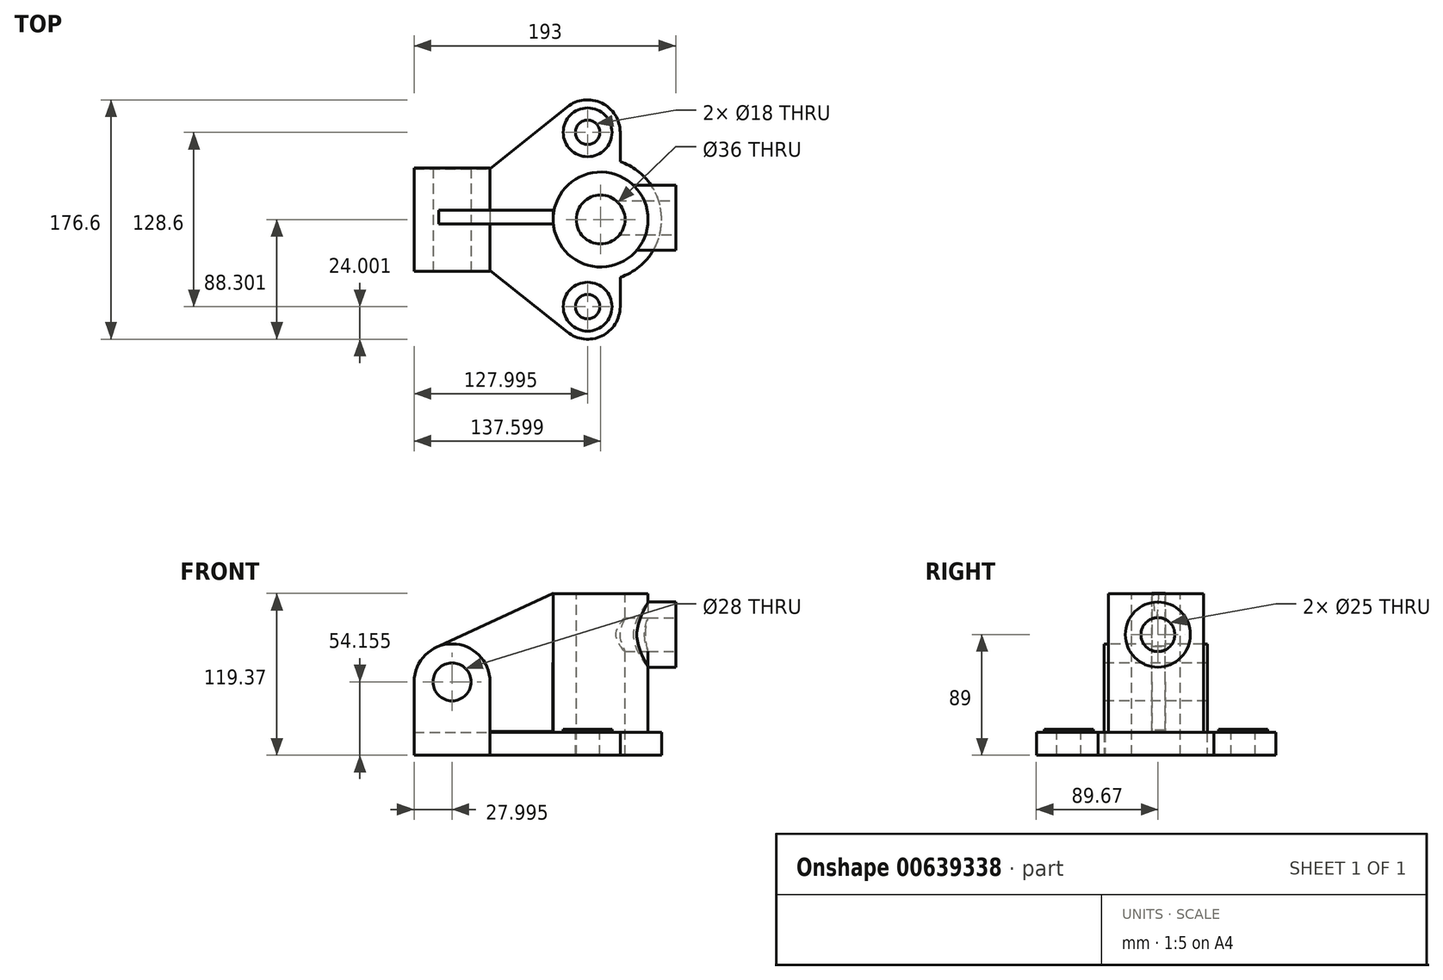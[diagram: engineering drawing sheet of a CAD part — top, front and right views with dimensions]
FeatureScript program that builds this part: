
annotation { "Feature Type Name" : "Feature", "Feature Type Description" : "" }
export const myFeature = defineFeature(function(context is Context, id is Id, definition is map)
    precondition{}
    {
        {
            var Q0;
            Q0=qCreatedBy(makeId("Top.planeOp"),FACE);
            var sketch = newSketch(context, id + "F0", { "sketchPlane" : qUnion([Q0])});
            skLineSegment(sketch, "E0.bottom", {"start": v(-54.34, 30.78) * mm, "end": v(1.66, 30.78) * mm});
            skLineSegment(sketch, "E0.top", {"start": v(-54.34, -44.22) * mm, "end": v(1.66, -44.22) * mm});
            skLineSegment(sketch, "E0.left", {"start": v(-54.34, 30.78) * mm, "end": v(-54.34, -44.22) * mm});
            skLineSegment(sketch, "E0.right", {"start": v(1.66, 30.78) * mm, "end": v(1.66, -44.22) * mm});
            skLineSegment(sketch, "E1", {"start": v(1.66, -44.22) * mm, "end": v(58.68, -89.77) * mm});
            skLineSegment(sketch, "E2", {"start": v(1.66, 30.78) * mm, "end": v(58.68, 76.33) * mm});
            skArc(sketch, "E3", {"start": v(58.68, 76.33) * mm, "mid": v(84.06, 79.2) * mm, "end": v(97.66, 57.58) * mm});
            skArc(sketch, "E4", {"start": v(58.68, -89.77) * mm, "mid": v(84.06, -92.65) * mm, "end": v(97.66, -71.02) * mm});
            skLineSegment(sketch, "E5", {"start": v(97.66, -71.02) * mm, "end": v(97.66, -49.35) * mm});
            skLineSegment(sketch, "E6", {"start": v(97.66, 57.58) * mm, "end": v(97.66, 35.92) * mm});
            skArc(sketch, "E7", {"start": v(97.66, -49.35) * mm, "mid": v(128.26, -6.72) * mm, "end": v(97.66, 35.92) * mm});
            skSolve(sketch);
        }
        {
            var Q0;
            Q0 = qSketchRegion(id + "F0", true);
            extrude(context, id + "F1", {"entities" : qUnion([Q0]), "depth" : 17 * mm, "offsetDistance" : 25.4 * mm});
        }
        {
            var Q0;
            Q0=makeQuery(id+"F1.opExtrude","CAP_FACE",FACE,{"disambiguationData":[OSD([sQuery(id+"F0.wireOp",EDGE,"E0.bottom"),sQuery(id+"F0.wireOp",EDGE,"E0.top"),sQuery(id+"F0.wireOp",EDGE,"E0.left"),sQuery(id+"F0.wireOp",EDGE,"E1"),sQuery(id+"F0.wireOp",EDGE,"E2"),sQuery(id+"F0.wireOp",EDGE,"E3"),sQuery(id+"F0.wireOp",EDGE,"E4"),sQuery(id+"F0.wireOp",EDGE,"E5"),sQuery(id+"F0.wireOp",EDGE,"E6"),sQuery(id+"F0.wireOp",EDGE,"E7")])],"isStart":false});
            var sketch = newSketch(context, id + "F2", { "sketchPlane" : qUnion([Q0])});
            skCircle(sketch, "E8", {"center": v(73.66, 57.58) * mm, "radius": 18 * mm});
            skCircle(sketch, "E9", {"center": v(73.66, -71.02) * mm, "radius": 18 * mm});
            skSolve(sketch);
        }
        {
            var Q0;
            Q0 = qSketchRegion(id + "F2", true);
            extrude(context, id + "F3", {"entities" : qUnion([Q0]), "operationType" : NewBodyOperationType.ADD, "depth" : 2 * mm, "offsetDistance" : 25.4 * mm});
        }
        {
            var Q0;
            Q0=makeQuery(id+"F3.opExtrude","CAP_FACE",FACE,{"disambiguationData":[OSD([sQuery(id+"F2.wireOp",EDGE,"E9")])],"isStart":false});
            var sketch = newSketch(context, id + "F4", { "sketchPlane" : qUnion([Q0])});
            skCircle(sketch, "E10", {"center": v(73.66, -71.02) * mm, "radius": 9 * mm});
            skCircle(sketch, "E11", {"center": v(73.66, 57.58) * mm, "radius": 9 * mm});
            skSolve(sketch);
        }
        {
            var Q0;
            Q0 = qSketchRegion(id + "F4", true);
            extrude(context, id + "F5", {"entities" : qUnion([Q0]), "operationType" : NewBodyOperationType.REMOVE, "oppositeDirection" : true, "depth" : 25.4 * mm, "offsetDistance" : 25.4 * mm});
        }
        {
            var Q0;
            Q0=makeQuery(id+"F1.opExtrude","CAP_FACE",FACE,{"disambiguationData":[OSD([sQuery(id+"F0.wireOp",EDGE,"E0.bottom"),sQuery(id+"F0.wireOp",EDGE,"E0.top"),sQuery(id+"F0.wireOp",EDGE,"E0.left"),sQuery(id+"F0.wireOp",EDGE,"E1"),sQuery(id+"F0.wireOp",EDGE,"E2"),sQuery(id+"F0.wireOp",EDGE,"E3"),sQuery(id+"F0.wireOp",EDGE,"E4"),sQuery(id+"F0.wireOp",EDGE,"E5"),sQuery(id+"F0.wireOp",EDGE,"E6"),sQuery(id+"F0.wireOp",EDGE,"E7")])],"isStart":false});
            var sketch = newSketch(context, id + "F6", { "sketchPlane" : qUnion([Q0])});
            skCircle(sketch, "E12", {"center": v(83.26, -6.72) * mm, "radius": 35 * mm});
            skSolve(sketch);
        }
        {
            var Q0;
            Q0 = qSketchRegion(id + "F6", true);
            extrude(context, id + "F7", {"entities" : qUnion([Q0]), "operationType" : NewBodyOperationType.ADD, "depth" : 102 * mm, "offsetDistance" : 25.4 * mm});
        }
        {
            var Q0;
            Q0=makeQuery(id+"F7.opExtrude","CAP_FACE",FACE,{"disambiguationData":[OSD([sQuery(id+"F6.wireOp",EDGE,"E12")])],"isStart":false});
            var sketch = newSketch(context, id + "F8", { "sketchPlane" : qUnion([Q0])});
            skCircle(sketch, "E13", {"center": v(83.26, -6.72) * mm, "radius": 18 * mm});
            skSolve(sketch);
        }
        {
            var Q0;
            Q0 = qSketchRegion(id + "F8", true);
            extrude(context, id + "F9", {"entities" : qUnion([Q0]), "operationType" : NewBodyOperationType.REMOVE, "oppositeDirection" : true, "depth" : 128.52 * mm, "offsetDistance" : 25.4 * mm});
        }
        {
            var Q0;
            Q0=makeQuery(id+"F1.opExtrude","SWEPT_FACE",FACE,{"disambiguationData":[OSD([sQuery(id+"F0.wireOp",EDGE,"E0.top")])]});
            extrude(context, id + "F10", {"entities" : qUnion([Q0]), "operationType" : NewBodyOperationType.ADD, "depth" : 0.76 * mm, "offsetDistance" : 25.4 * mm});
        }
        {
            var Q0;
            Q0=makeQuery(id+"F10.opExtrude","CAP_FACE",FACE,{"disambiguationData":[OSD([sQuery(id+"F0.wireOp",EDGE,"E0.top")])],"isStart":false});
            var sketch = newSketch(context, id + "F11", { "sketchPlane" : qUnion([Q0])});
            skLineSegment(sketch, "E14", {"start": v(-54.34, 8.5) * mm, "end": v(-54.34, 54.16) * mm});
            skPoint(sketch, "E14.startSnap0", {"position": v(-54.34, 8.5) * mm});
            skArc(sketch, "E15", {"start": v(-54.34, 54.16) * mm, "mid": v(-26.34, 82.16) * mm, "end": v(1.66, 54.16) * mm});
            skLineSegment(sketch, "E16", {"start": v(1.66, 54.16) * mm, "end": v(1.66, 17) * mm});
            skLineSegment(sketch, "E17", {"start": v(1.66, 17) * mm, "end": v(-54.34, 17) * mm});
            skSolve(sketch);
        }
        {
            var Q0;
            Q0 = qSketchRegion(id + "F11", true);
            extrude(context, id + "F12", {"entities" : qUnion([Q0]), "operationType" : NewBodyOperationType.ADD, "oppositeDirection" : true, "depth" : 76.2 * mm, "offsetDistance" : 25.4 * mm});
        }
        {
            var Q0;
            Q0=makeQuery(id+"F12.boolean.opBoolean","MERGE",FACE,{"derivedFrom":[makeQuery(id+"F10.opExtrude","CAP_FACE",FACE,{"disambiguationData":[OSD([sQuery(id+"F0.wireOp",EDGE,"E0.top")])],"isStart":false}),makeQuery(id+"F12.opExtrude","CAP_FACE",FACE,{"disambiguationData":[OSD([sQuery(id+"F11.wireOp",EDGE,"E14"),sQuery(id+"F11.wireOp",EDGE,"E15"),sQuery(id+"F11.wireOp",EDGE,"E16"),sQuery(id+"F11.wireOp",EDGE,"E17")])],"isStart":true})]});
            var sketch = newSketch(context, id + "F13", { "sketchPlane" : qUnion([Q0])});
            skCircle(sketch, "E18", {"center": v(-26.34, 54.16) * mm, "radius": 14 * mm});
            skSolve(sketch);
        }
        {
            var Q0;
            Q0 = qSketchRegion(id + "F13", true);
            extrude(context, id + "F14", {"entities" : qUnion([Q0]), "operationType" : NewBodyOperationType.REMOVE, "oppositeDirection" : true, "depth" : 167.39 * mm, "offsetDistance" : 25.4 * mm});
        }
        {
            var Q0;
            Q0=qCreatedBy(makeId("Front.planeOp"),FACE);
            var sketch = newSketch(context, id + "F15", { "sketchPlane" : qUnion([Q0])});
            skLineSegment(sketch, "E19", {"start": v(48.3, 119.37) * mm, "end": v(-36.3, 80.4) * mm});
            skLineSegment(sketch, "E20", {"start": v(-36.3, 80.4) * mm, "end": v(-5.27, 60.76) * mm});
            skLineSegment(sketch, "E21", {"start": v(-5.27, 60.76) * mm, "end": v(1.8, 17.55) * mm});
            skLineSegment(sketch, "E22", {"start": v(1.8, 17.55) * mm, "end": v(48.04, 17.55) * mm});
            skLineSegment(sketch, "E23", {"start": v(48.04, 17.55) * mm, "end": v(48.3, 119.37) * mm});
            skSolve(sketch);
        }
        {
            var Q0;
            Q0 = qSketchRegion(id + "F15", true);
            extrude(context, id + "F16", {"entities" : qUnion([Q0]), "operationType" : NewBodyOperationType.ADD, "depth" : 9.9 * mm, "offsetDistance" : 25.4 * mm});
        }
        {
            var Q0;
            {var subQ0=sQuery(id+"F0.wireOp",EDGE,"E0.left");Q0=makeQuery(id+"F12.boolean.opBoolean","MERGE",FACE,{"derivedFrom":[makeQuery(id+"F10.boolean.opBoolean","MERGE",FACE,{"derivedFrom":[makeQuery(id+"F1.opExtrude","SWEPT_FACE",FACE,{"disambiguationData":[OSD([subQ0])]}),makeQuery(id+"F10.opExtrude","SWEPT_FACE",FACE,{"disambiguationData":[OSD([sQuery(id+"F0.wireOp",EDGE,"E0.top"),subQ0])]})]}),makeQuery(id+"F12.opExtrude","SWEPT_FACE",FACE,{"disambiguationData":[OSD([sQuery(id+"F11.wireOp",EDGE,"E14")])]})]});}
            cPlane(context, id + "F17", {"entities" : qUnion([Q0]), "cplaneType" : CPlaneType.OFFSET, "offset" : 193 * mm, "oppositeDirection" : true, "width" : 152.4 * mm, "height" : 152.4 * mm});
        }
        {
            var Q0;
            Q0=qCreatedBy(id+"F17.planeOp",FACE);
            var sketch = newSketch(context, id + "F18", { "sketchPlane" : qUnion([Q0])});
            skCircle(sketch, "E24", {"center": v(5.35, 89) * mm, "radius": 24 * mm});
            skSolve(sketch);
        }
        {
            var Q0;
            Q0=makeQuery(id+"F18.imprint","IMPRINT",FACE,{"disambiguationData":[TD([[makeQuery(id+"F18.imprint","IMPRINT",EDGE,{"derivedFrom":sQuery(id+"F18.wireOp",EDGE,"E24")}),1.0]])]});
            extrude(context, id + "F19", {"entities" : qUnion([Q0]), "endBound" : BoundingType.UP_TO_NEXT, "depth" : 25.4 * mm, "offsetDistance" : 25.4 * mm});
        }
        {
            var Q0;
            Q0=makeQuery(id+"F19.opExtrude","CAP_FACE",FACE,{"disambiguationData":[OSD([sQuery(id+"F18.wireOp",EDGE,"E24")])],"isStart":true});
            var sketch = newSketch(context, id + "F20", { "sketchPlane" : qUnion([Q0])});
            skCircle(sketch, "E25", {"center": v(-5.35, 89) * mm, "radius": 12.5 * mm});
            skSolve(sketch);
        }
        {
            var Q0;
            Q0 = qSketchRegion(id + "F20", true);
            extrude(context, id + "F21", {"entities" : qUnion([Q0]), "operationType" : NewBodyOperationType.REMOVE, "oppositeDirection" : true, "depth" : 53.1 * mm, "offsetDistance" : 25.4 * mm});
        }
    });
